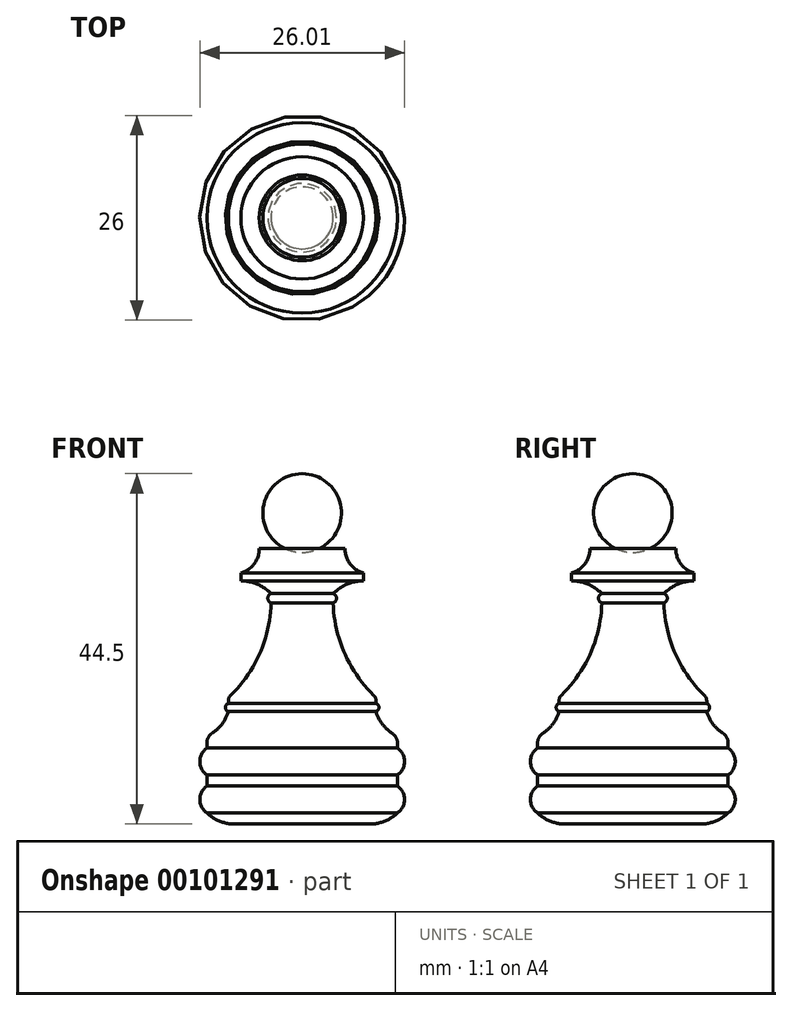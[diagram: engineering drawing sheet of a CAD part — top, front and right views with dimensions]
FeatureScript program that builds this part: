
annotation { "Feature Type Name" : "Feature", "Feature Type Description" : "" }
export const myFeature = defineFeature(function(context is Context, id is Id, definition is map)
    precondition{}
    {
        {
            var Q0;
            Q0=qCreatedBy(makeId("Front.planeOp"),FACE);
            var sketch = newSketch(context, id + "F0", { "sketchPlane" : qUnion([Q0])});
            skLineSegment(sketch, "E0", {"start": v(-277.8, 59.26) * mm, "end": v(-277.8, 24.26) * mm});
            skLineSegment(sketch, "E1", {"start": v(-277.8, 24.26) * mm, "end": v(-265.7, 24.26) * mm});
            skLineSegment(sketch, "E2", {"start": v(-265.7, 24.26) * mm, "end": v(-265.7, 25.67) * mm});
            skLineSegment(sketch, "E3", {"start": v(-277.8, 59.26) * mm, "end": v(-272.35, 59.26) * mm});
            skLineSegment(sketch, "E4", {"start": v(-272.35, 59.26) * mm, "end": v(-272.35, 56.14) * mm});
            skLineSegment(sketch, "E5", {"start": v(-272.35, 56.14) * mm, "end": v(-270.03, 56.14) * mm});
            skLineSegment(sketch, "E6", {"start": v(-270.03, 56.14) * mm, "end": v(-270.03, 55.14) * mm});
            skLineSegment(sketch, "E7", {"start": v(-270.03, 55.14) * mm, "end": v(-273.86, 55.14) * mm});
            skLineSegment(sketch, "E8", {"start": v(-273.86, 55.14) * mm, "end": v(-273.86, 53.51) * mm});
            skArc(sketch, "E9", {"start": v(-273.86, 52.36) * mm, "mid": v(-273.42, 52.94) * mm, "end": v(-273.86, 53.51) * mm});
            skLineSegment(sketch, "E10", {"start": v(-273.86, 52.36) * mm, "end": v(-273.86, 40.9) * mm});
            skLineSegment(sketch, "E11", {"start": v(-273.86, 40.9) * mm, "end": v(-268.42, 40.9) * mm});
            skLineSegment(sketch, "E12", {"start": v(-268.42, 40.9) * mm, "end": v(-268.42, 39.56) * mm});
            skArc(sketch, "E13", {"start": v(-268.42, 38.56) * mm, "mid": v(-268.05, 39.06) * mm, "end": v(-268.42, 39.56) * mm});
            skLineSegment(sketch, "E14", {"start": v(-268.42, 38.56) * mm, "end": v(-268.42, 36.04) * mm});
            skArc(sketch, "E15", {"start": v(-265.7, 25.67) * mm, "mid": v(-264.8, 27.37) * mm, "end": v(-265.7, 29.08) * mm});
            skLineSegment(sketch, "E16", {"start": v(-265.7, 29.08) * mm, "end": v(-265.7, 30.49) * mm});
            skArc(sketch, "E17", {"start": v(-265.7, 30.49) * mm, "mid": v(-264.8, 32.2) * mm, "end": v(-265.7, 33.9) * mm});
            skLineSegment(sketch, "E18", {"start": v(-265.7, 33.9) * mm, "end": v(-265.7, 36.04) * mm});
            skLineSegment(sketch, "E19", {"start": v(-265.7, 36.04) * mm, "end": v(-268.42, 36.04) * mm});
            skSolve(sketch);
        }
        {
            var Q0;
            Q0=makeQuery(id+"F0.imprint","IMPRINT",FACE,{"disambiguationData":[TD([[makeQuery(id+"F0.imprint","IMPRINT",EDGE,{"derivedFrom":sQuery(id+"F0.wireOp",EDGE,"E0")}),1.0]])]});
            var Q1;
            Q1=sQuery(id+"F0.wireOp",EDGE,"E0");
            revolve(context, id + "F1", {"entities" : qUnion([Q0]), "axis" : qUnion([Q1]), "revolveType" : RevolveType.FULL});
        }
        {
            var Q0;
            Q0=makeQuery(id+"F1.opRevolve","SWEPT_EDGE",EDGE,{"disambiguationData":[OSD([sQuery(id+"F0.wireOp",EDGE,"E1"),sQuery(id+"F0.wireOp",EDGE,"E2")])]});
            fillet(context, id + "F2", {"entities" : qUnion([Q0]), "radius" : 5 * mm, "tangentPropagation" : true, "allowEdgeOverflow" : false});
        }
        {
            var Q0;
            Q0=makeQuery(id+"F1.opRevolve","SWEPT_EDGE",EDGE,{"disambiguationData":[OSD([sQuery(id+"F0.wireOp",EDGE,"E18"),sQuery(id+"F0.wireOp",EDGE,"E19")])]});
            fillet(context, id + "F3", {"entities" : qUnion([Q0]), "radius" : 1.5 * mm, "tangentPropagation" : true, "allowEdgeOverflow" : false});
        }
        {
            var Q0;
            Q0=makeQuery(id+"F1.opRevolve","SWEPT_EDGE",EDGE,{"disambiguationData":[OSD([sQuery(id+"F0.wireOp",EDGE,"E14"),sQuery(id+"F0.wireOp",EDGE,"E19")])]});
            fillet(context, id + "F4", {"entities" : qUnion([Q0]), "radius" : 5 * mm, "tangentPropagation" : true, "allowEdgeOverflow" : false});
        }
        {
            var Q0;
            Q0=makeQuery(id+"F1.opRevolve","SWEPT_EDGE",EDGE,{"disambiguationData":[OSD([sQuery(id+"F0.wireOp",EDGE,"E11"),sQuery(id+"F0.wireOp",EDGE,"E12")])]});
            fillet(context, id + "F5", {"entities" : qUnion([Q0]), "radius" : 1 * mm, "tangentPropagation" : true, "allowEdgeOverflow" : false});
        }
        {
            var Q0;
            Q0=makeQuery(id+"F1.opRevolve","SWEPT_EDGE",EDGE,{"disambiguationData":[OSD([sQuery(id+"F0.wireOp",EDGE,"E10"),sQuery(id+"F0.wireOp",EDGE,"E11")])]});
            fillet(context, id + "F6", {"entities" : qUnion([Q0]), "radius" : 17 * mm, "tangentPropagation" : true, "allowEdgeOverflow" : false});
        }
        {
            var Q0;
            Q0=makeQuery(id+"F1.opRevolve","SWEPT_EDGE",EDGE,{"disambiguationData":[OSD([sQuery(id+"F0.wireOp",EDGE,"E7"),sQuery(id+"F0.wireOp",EDGE,"E8")])]});
            fillet(context, id + "F7", {"entities" : qUnion([Q0]), "radius" : 5.3 * mm, "tangentPropagation" : true, "allowEdgeOverflow" : false});
        }
        {
            var Q0;
            Q0=makeQuery(id+"F1.opRevolve","SWEPT_EDGE",EDGE,{"disambiguationData":[OSD([sQuery(id+"F0.wireOp",EDGE,"E4"),sQuery(id+"F0.wireOp",EDGE,"E5")])]});
            fillet(context, id + "F8", {"entities" : qUnion([Q0]), "radius" : 3.25 * mm, "tangentPropagation" : true, "allowEdgeOverflow" : false});
        }
        {
            var Q0;
            Q0=makeQuery(id+"F1.opRevolve","SWEPT_FACE",FACE,{"disambiguationData":[OSD([sQuery(id+"F0.wireOp",EDGE,"E3")])]});
            cPlane(context, id + "F9", {"entities" : qUnion([Q0]), "cplaneType" : CPlaneType.OFFSET, "offset" : 0.5 * mm, "oppositeDirection" : true, "width" : 150 * mm, "height" : 150 * mm});
        }
        {
            var Q0;
            Q0=qCreatedBy(id+"F9.planeOp",FACE);
            var sketch = newSketch(context, id + "F10", { "sketchPlane" : qUnion([Q0])});
            skCircle(sketch, "E20", {"center": v(-277.8, 0) * mm, "radius": 5 * mm});
            skSolve(sketch);
        }
        {
            var Q0;
            Q0=makeQuery(id+"F10.imprint","IMPRINT",FACE,{"disambiguationData":[TD([[makeQuery(id+"F10.imprint","IMPRINT",EDGE,{"derivedFrom":sQuery(id+"F10.wireOp",EDGE,"E20")}),1.0]])]});
            extrude(context, id + "F11", {"entities" : qUnion([Q0]), "depth" : 10 * mm});
        }
        {
            var Q0;
            Q0=makeQuery(id+"F11.opExtrude","CAP_EDGE",EDGE,{"disambiguationData":[OSD([sQuery(id+"F10.wireOp",EDGE,"E20")])],"isStart":false});
            var Q1;
            Q1=makeQuery(id+"F11.opExtrude","CAP_EDGE",EDGE,{"disambiguationData":[OSD([sQuery(id+"F10.wireOp",EDGE,"E20")])],"isStart":true});
            fillet(context, id + "F12", {"entities" : qUnion([Q0, Q1]), "radius" : 5 * mm, "tangentPropagation" : true, "allowEdgeOverflow" : false});
        }
    });
